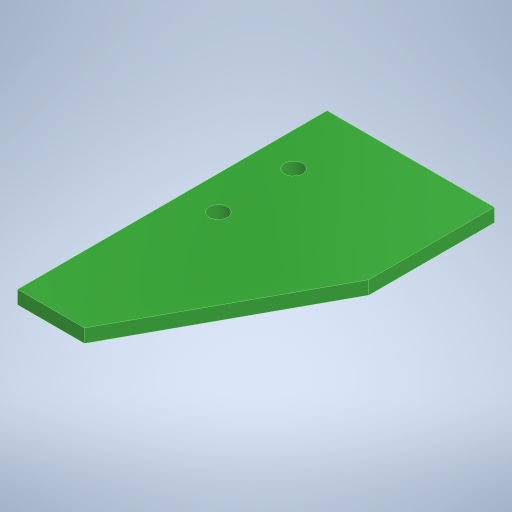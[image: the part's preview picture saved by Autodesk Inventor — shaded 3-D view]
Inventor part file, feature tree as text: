
AUTODESK INVENTOR PART (.ipt)
format: ipt  version: 2024.1 (Build 281209000, 209)  size: 236,544 bytes
history: native  units: in
note: dims shown in document units (in); Inventor stores cm internally (conversion verified against a paired STEP export)
features: extrude x2, sketch x2
ambient origin geometry x8: Origin, YZ Plane, XZ Plane, XY Plane, X Axis, Y Axis, Z Axis, Center Point
bodies: Solid1 (feature_tree)
feature tree (4):
  extrude  "Extrusion1"  Depth=1.4567in
  extrude  "Extrusion2"  Depth=0.063in
  sketch  "Sketch1"  dims[d0=1.4567in d1=0.315in]
  sketch  "Sketch2"  dims[d2=0.7874in d3=0.5906in d4=0.063in d5=0.0in d6=0.0866in d7=0.0866in d8=0.1575in d9=0.1575in d10=0.315in d11=0.3543in d12=0.0in d13=0.0in]
